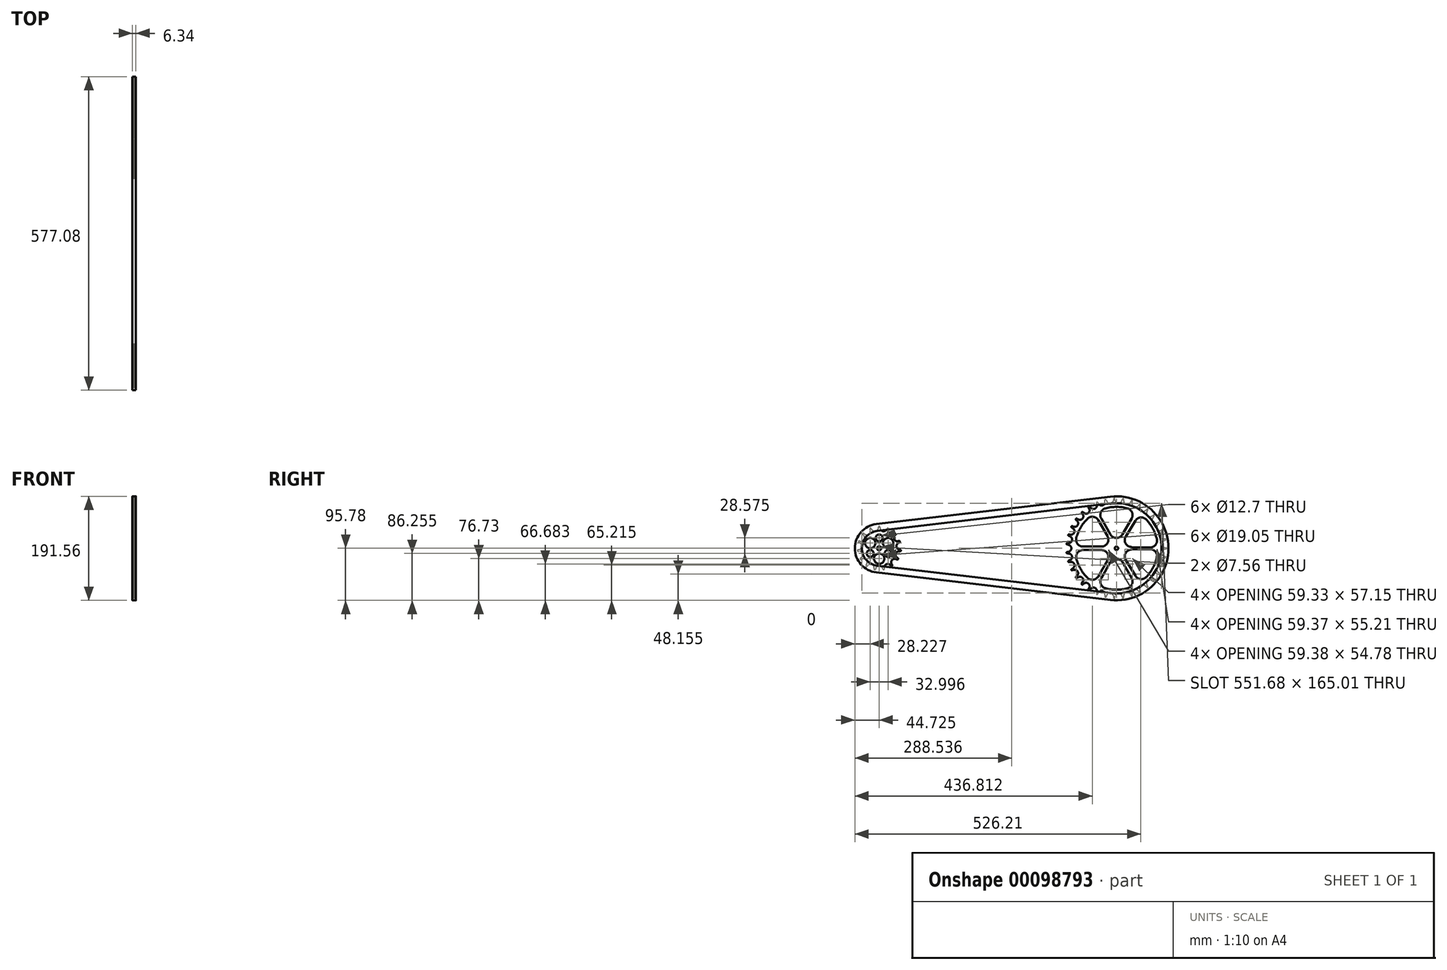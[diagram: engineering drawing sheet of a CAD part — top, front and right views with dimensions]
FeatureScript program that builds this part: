
annotation { "Feature Type Name" : "Feature", "Feature Type Description" : "" }
export const myFeature = defineFeature(function(context is Context, id is Id, definition is map)
    precondition{}
    {
        {
            var Q0;
            Q0=qCreatedBy(makeId("Right.planeOp"),FACE);
            var sketch = newSketch(context, id + "F0", { "sketchPlane" : qUnion([Q0])});
            skPoint(sketch, "E0.0.midPoint", {"position": v(88.9, 0) * mm});
            skArc(sketch, "E1", {"start": v(-53.39, 54.37) * mm, "mid": v(-66, 38.1) * mm, "end": v(-73.78, 19.05) * mm});
            skLineSegment(sketch, "E2", {"start": v(-33.5, 51.66) * mm, "end": v(-16.5, 22.22) * mm});
            skLineSegment(sketch, "E3", {"start": v(-61.48, 3.18) * mm, "end": v(-27.5, 3.18) * mm});
            skArc(sketch, "E4", {"start": v(-27.5, 3.17) * mm, "mid": v(-16.5, 9.52) * mm, "end": v(-16.5, 22.23) * mm});
            skArc(sketch, "E5", {"start": v(-33.5, 51.66) * mm, "mid": v(-42.77, 57.9) * mm, "end": v(-53.39, 54.37) * mm});
            skArc(sketch, "E6", {"start": v(-73.78, 19.05) * mm, "mid": v(-71.52, 8.1) * mm, "end": v(-61.48, 3.17) * mm});
            skArc(sketch, "E7.MirrorCS", {"start": v(-20.4, 73.42) * mm, "mid": v(0, 76.2) * mm, "end": v(20.4, 73.42) * mm});
            skArc(sketch, "E8.MirrorCS", {"start": v(-28, 54.83) * mm, "mid": v(-28.75, 66) * mm, "end": v(-20.4, 73.42) * mm});
            skLineSegment(sketch, "E9.MirrorCS", {"start": v(-28, 54.83) * mm, "end": v(-11, 25.4) * mm});
            skArc(sketch, "E10.MirrorCS", {"start": v(11, 25.4) * mm, "mid": v(0, 19.05) * mm, "end": v(-11, 25.4) * mm});
            skLineSegment(sketch, "E11.MirrorCS", {"start": v(28, 54.83) * mm, "end": v(11, 25.4) * mm});
            skArc(sketch, "E12.MirrorCS", {"start": v(20.4, 73.42) * mm, "mid": v(28.75, 66) * mm, "end": v(28, 54.83) * mm});
            skArc(sketch, "E13.MirrorCS", {"start": v(74.27, 17.03) * mm, "mid": v(67, 36.28) * mm, "end": v(54.85, 52.9) * mm});
            skArc(sketch, "E14.MirrorCS", {"start": v(61.55, 1.5) * mm, "mid": v(71.72, 6.14) * mm, "end": v(74.27, 17.03) * mm});
            skLineSegment(sketch, "E15.MirrorCS", {"start": v(61.55, 1.5) * mm, "end": v(27.57, 2.42) * mm});
            skArc(sketch, "E16.MirrorCS", {"start": v(17.1, 21.77) * mm, "mid": v(16.75, 9.07) * mm, "end": v(27.57, 2.42) * mm});
            skLineSegment(sketch, "E17.MirrorCS", {"start": v(34.9, 50.72) * mm, "end": v(17.1, 21.77) * mm});
            skArc(sketch, "E18.MirrorCS", {"start": v(54.85, 52.9) * mm, "mid": v(44.34, 56.7) * mm, "end": v(34.9, 50.72) * mm});
            skArc(sketch, "E19.MirrorCS", {"start": v(-53.39, -54.37) * mm, "mid": v(-66, -38.1) * mm, "end": v(-73.78, -19.05) * mm});
            skArc(sketch, "E20.MirrorCS", {"start": v(-73.78, -19.05) * mm, "mid": v(-71.52, -8.1) * mm, "end": v(-61.48, -3.17) * mm});
            skLineSegment(sketch, "E21.MirrorCS", {"start": v(-61.48, -3.18) * mm, "end": v(-27.5, -3.18) * mm});
            skArc(sketch, "E22.MirrorCS", {"start": v(-27.5, -3.17) * mm, "mid": v(-16.5, -9.52) * mm, "end": v(-16.5, -22.23) * mm});
            skLineSegment(sketch, "E23.MirrorCS", {"start": v(-33.5, -51.66) * mm, "end": v(-16.5, -22.22) * mm});
            skArc(sketch, "E24.MirrorCS", {"start": v(-33.5, -51.66) * mm, "mid": v(-42.77, -57.9) * mm, "end": v(-53.39, -54.37) * mm});
            skArc(sketch, "E25.MirrorCS", {"start": v(-28, -54.83) * mm, "mid": v(-28.75, -66) * mm, "end": v(-20.4, -73.42) * mm});
            skArc(sketch, "E26.MirrorCS", {"start": v(-20.4, -73.42) * mm, "mid": v(0, -76.2) * mm, "end": v(20.4, -73.42) * mm});
            skArc(sketch, "E27.MirrorCS", {"start": v(20.4, -73.42) * mm, "mid": v(28.75, -66) * mm, "end": v(28, -54.83) * mm});
            skLineSegment(sketch, "E28.MirrorCS", {"start": v(28, -54.83) * mm, "end": v(11, -25.4) * mm});
            skArc(sketch, "E29.MirrorCS", {"start": v(11, -25.4) * mm, "mid": v(0, -19.05) * mm, "end": v(-11, -25.4) * mm});
            skLineSegment(sketch, "E30.MirrorCS", {"start": v(34.9, -50.72) * mm, "end": v(17.1, -21.77) * mm});
            skArc(sketch, "E31.MirrorCS", {"start": v(54.85, -52.9) * mm, "mid": v(44.34, -56.7) * mm, "end": v(34.9, -50.72) * mm});
            skArc(sketch, "E32.MirrorCS", {"start": v(74.27, -17.03) * mm, "mid": v(67, -36.28) * mm, "end": v(54.85, -52.9) * mm});
            skArc(sketch, "E33.MirrorCS", {"start": v(61.55, -1.5) * mm, "mid": v(71.72, -6.14) * mm, "end": v(74.27, -17.03) * mm});
            skLineSegment(sketch, "E34.MirrorCS", {"start": v(61.55, -1.5) * mm, "end": v(27.57, -2.42) * mm});
            skArc(sketch, "E35.MirrorCS", {"start": v(17.1, -21.77) * mm, "mid": v(16.75, -9.07) * mm, "end": v(27.57, -2.42) * mm});
            skLineSegment(sketch, "E36.MirrorCS", {"start": v(-28, -54.83) * mm, "end": v(-11, -25.4) * mm});
            skArc(sketch, "E37", {"start": v(-62.06, 66.67) * mm, "mid": v(-63.62, 66.56) * mm, "end": v(-63.79, 65.01) * mm});
            skArc(sketch, "E38.trimOffspring", {"start": v(-70.02, 53.03) * mm, "mid": v(-62.46, 54.56) * mm, "end": v(-61.95, 62.26) * mm});
            skArc(sketch, "E39.MirrorCS", {"start": v(-74.4, 52.54) * mm, "mid": v(-74.5, 54.1) * mm, "end": v(-72.99, 54.48) * mm});
            skPoint(sketch, "E40.orphan", {"position": v(-81.26, 58.5) * mm});
            skArc(sketch, "E41.MirrorCS", {"start": v(-36.12, 80.06) * mm, "mid": v(-39.3, 73.03) * mm, "end": v(-46.92, 74.26) * mm});
            skArc(sketch, "E42.MirrorCS", {"start": v(-51.18, 75.34) * mm, "mid": v(-50.74, 76.83) * mm, "end": v(-49.19, 76.65) * mm});
            skArc(sketch, "E43", {"start": v(-59.4, 64.7) * mm, "mid": v(-51.8, 64.95) * mm, "end": v(-49.87, 72.3) * mm});
            skArc(sketch, "E44.MirrorCS", {"start": v(-34.67, 84.22) * mm, "mid": v(-36.16, 84.68) * mm, "end": v(-36.87, 83.28) * mm});
            skPoint(sketch, "E45.orphan", {"position": v(-38.96, 92.24) * mm});
            skArc(sketch, "E46.MirrorCS", {"start": v(-21.28, 85.22) * mm, "mid": v(-25.66, 79) * mm, "end": v(-32.86, 81.46) * mm});
            skArc(sketch, "E47.MirrorCS", {"start": v(-21.44, 88.52) * mm, "mid": v(-20.5, 89.76) * mm, "end": v(-19.1, 89.05) * mm});
            skArc(sketch, "E48.MirrorCS", {"start": v(-5.68, 87.65) * mm, "mid": v(-11.12, 82.18) * mm, "end": v(-17.83, 86) * mm});
            skArc(sketch, "E49.MirrorCS", {"start": v(-2.86, 91.03) * mm, "mid": v(-4.1, 91.98) * mm, "end": v(-5.25, 90.93) * mm});
            skArc(sketch, "E50.MirrorCS", {"start": v(-84.2, 25.04) * mm, "mid": v(-77.65, 29.13) * mm, "end": v(-79.88, 36.52) * mm});
            skArc(sketch, "E51.MirrorCS", {"start": v(-72.1, 50.17) * mm, "mid": v(-71.31, 42.6) * mm, "end": v(-78.35, 39.7) * mm});
            skArc(sketch, "E52.MirrorCS", {"start": v(-81.53, 40.6) * mm, "mid": v(-82.95, 39.96) * mm, "end": v(-82.57, 38.45) * mm});
            skArc(sketch, "E53.MirrorCS", {"start": v(-88.12, 23.04) * mm, "mid": v(-88.77, 24.46) * mm, "end": v(-87.48, 25.35) * mm});
            skArc(sketch, "E54.MirrorCS", {"start": v(-87.3, 9.64) * mm, "mid": v(-81.74, 14.82) * mm, "end": v(-85.13, 21.63) * mm});
            skArc(sketch, "E55.MirrorCS", {"start": v(-90.6, 9.36) * mm, "mid": v(-91.7, 8.26) * mm, "end": v(-90.81, 6.98) * mm});
            skArc(sketch, "E56.MirrorCS", {"start": v(-87.62, -6.15) * mm, "mid": v(-82.93, -0.02) * mm, "end": v(-87.62, 6.11) * mm});
            skArc(sketch, "E57.MirrorCS", {"start": v(-90.6, -9.4) * mm, "mid": v(-91.7, -8.3) * mm, "end": v(-90.8, -7) * mm});
            skArc(sketch, "E58.MirrorCS", {"start": v(-87.31, -9.62) * mm, "mid": v(-81.75, -14.8) * mm, "end": v(-85.15, -21.6) * mm});
            skArc(sketch, "E59.MirrorCS", {"start": v(-88.14, -23.02) * mm, "mid": v(-88.8, -24.44) * mm, "end": v(-87.5, -25.33) * mm});
            skArc(sketch, "E60.MirrorCS", {"start": v(-84.22, -25.02) * mm, "mid": v(-77.68, -29.12) * mm, "end": v(-79.92, -36.5) * mm});
            skArc(sketch, "E61.MirrorCS", {"start": v(-81.57, -40.59) * mm, "mid": v(-83, -39.94) * mm, "end": v(-82.6, -38.43) * mm});
            skArc(sketch, "E62.MirrorCS", {"start": v(-72.1, -50.18) * mm, "mid": v(-71.32, -42.61) * mm, "end": v(-78.36, -39.72) * mm});
            skArc(sketch, "E63.MirrorCS", {"start": v(-74.42, -52.5) * mm, "mid": v(-74.53, -54.06) * mm, "end": v(-73.02, -54.44) * mm});
            skArc(sketch, "E64.MirrorCS", {"start": v(-70.05, -53) * mm, "mid": v(-62.48, -54.53) * mm, "end": v(-61.99, -62.23) * mm});
            skArc(sketch, "E65.MirrorCS", {"start": v(-62.1, -66.63) * mm, "mid": v(-63.65, -66.53) * mm, "end": v(-63.82, -64.98) * mm});
            skArc(sketch, "E66.MirrorCS", {"start": v(-59.43, -64.68) * mm, "mid": v(-51.83, -64.92) * mm, "end": v(-49.91, -72.28) * mm});
            skArc(sketch, "E67.MirrorCS", {"start": v(-51.23, -75.3) * mm, "mid": v(-50.78, -76.8) * mm, "end": v(-49.23, -76.63) * mm});
            skArc(sketch, "E68.MirrorCS", {"start": v(-46.96, -74.23) * mm, "mid": v(-39.34, -73) * mm, "end": v(-36.16, -80.04) * mm});
            skArc(sketch, "E69.MirrorCS", {"start": v(-21.28, -85.22) * mm, "mid": v(-25.67, -79) * mm, "end": v(-32.87, -81.45) * mm});
            skArc(sketch, "E70.MirrorCS", {"start": v(-34.67, -84.22) * mm, "mid": v(-36.17, -84.67) * mm, "end": v(-36.87, -83.28) * mm});
            skArc(sketch, "E71.MirrorCS", {"start": v(-21.45, -88.52) * mm, "mid": v(-20.5, -89.76) * mm, "end": v(-19.11, -89.05) * mm});
            skArc(sketch, "E72.MirrorCS", {"start": v(-5.68, -87.65) * mm, "mid": v(-11.13, -82.18) * mm, "end": v(-17.83, -86) * mm});
            skArc(sketch, "E73.MirrorCS", {"start": v(-2.86, -91.03) * mm, "mid": v(-4.1, -91.98) * mm, "end": v(-5.25, -90.93) * mm});
            skArc(sketch, "E74.MirrorCS", {"start": v(-2.2, -87.82) * mm, "mid": v(3.69, -83) * mm, "end": v(9.97, -87.28) * mm});
            skArc(sketch, "E75.MirrorCS", {"start": v(11.02, -90.44) * mm, "mid": v(12.34, -91.28) * mm, "end": v(13.4, -90.12) * mm});
            skArc(sketch, "E76.MirrorCS", {"start": v(13.48, -86.8) * mm, "mid": v(18.41, -80.86) * mm, "end": v(25.43, -84.07) * mm});
            skArc(sketch, "E77.MirrorCS", {"start": v(29.26, -86.25) * mm, "mid": v(28.43, -87.58) * mm, "end": v(26.98, -86.99) * mm});
            skArc(sketch, "E78.MirrorCS", {"start": v(28.8, -82.98) * mm, "mid": v(32.61, -76.4) * mm, "end": v(40, -78.2) * mm});
            skArc(sketch, "E79.MirrorCS", {"start": v(42.05, -80.8) * mm, "mid": v(43.58, -81.1) * mm, "end": v(44.16, -79.66) * mm});
            skArc(sketch, "E80.MirrorCS", {"start": v(53.4, -69.74) * mm, "mid": v(45.7, -69.2) * mm, "end": v(43.16, -76.5) * mm});
            skArc(sketch, "E81.MirrorCS", {"start": v(57.74, -70.44) * mm, "mid": v(57.43, -71.97) * mm, "end": v(55.87, -71.93) * mm});
            skArc(sketch, "E82.MirrorCS", {"start": v(64.96, -59.12) * mm, "mid": v(57.41, -60.03) * mm, "end": v(56.16, -67.54) * mm});
            skArc(sketch, "E83.MirrorCS", {"start": v(67.8, -60.82) * mm, "mid": v(69.34, -60.58) * mm, "end": v(69.37, -59.02) * mm});
            skArc(sketch, "E84.MirrorCS", {"start": v(74.5, -46.53) * mm, "mid": v(67.1, -48.73) * mm, "end": v(67.3, -56.45) * mm});
            skArc(sketch, "E85.MirrorCS", {"start": v(-2.14, 87.8) * mm, "mid": v(3.74, 82.99) * mm, "end": v(10.03, 87.26) * mm});
            skArc(sketch, "E86.MirrorCS", {"start": v(11.03, 90.4) * mm, "mid": v(12.35, 91.24) * mm, "end": v(13.4, 90.09) * mm});
            skArc(sketch, "E87.MirrorCS", {"start": v(13.54, 86.79) * mm, "mid": v(18.47, 80.85) * mm, "end": v(25.49, 84.06) * mm});
            skArc(sketch, "E88.MirrorCS", {"start": v(29.32, 86.23) * mm, "mid": v(28.49, 87.56) * mm, "end": v(27.04, 86.97) * mm});
            skArc(sketch, "E89.MirrorCS", {"start": v(40.06, 78.17) * mm, "mid": v(32.67, 76.38) * mm, "end": v(28.86, 82.96) * mm});
            skArc(sketch, "E90.MirrorCS", {"start": v(42.1, 80.76) * mm, "mid": v(43.63, 81.08) * mm, "end": v(44.21, 79.63) * mm});
            skArc(sketch, "E91.MirrorCS", {"start": v(53.4, 69.74) * mm, "mid": v(45.7, 69.2) * mm, "end": v(43.17, 76.5) * mm});
            skArc(sketch, "E92.MirrorCS", {"start": v(56.17, 67.53) * mm, "mid": v(57.42, 60.03) * mm, "end": v(64.97, 59.1) * mm});
            skArc(sketch, "E93.MirrorCS", {"start": v(57.75, 70.43) * mm, "mid": v(57.44, 71.96) * mm, "end": v(55.88, 71.92) * mm});
            skArc(sketch, "E94.MirrorCS", {"start": v(67.8, 60.81) * mm, "mid": v(69.34, 60.57) * mm, "end": v(69.38, 59.01) * mm});
            skArc(sketch, "E95.MirrorCS", {"start": v(74.5, 46.52) * mm, "mid": v(67.1, 48.72) * mm, "end": v(67.3, 56.44) * mm});
            skArc(sketch, "E96.MirrorCS", {"start": v(78.82, 45.64) * mm, "mid": v(79.07, 47.18) * mm, "end": v(77.6, 47.7) * mm});
            skArc(sketch, "E97.MirrorCS", {"start": v(81.6, 32.5) * mm, "mid": v(74.86, 36.02) * mm, "end": v(76.32, 43.48) * mm});
            skArc(sketch, "E98.MirrorCS", {"start": v(84.85, 33.1) * mm, "mid": v(86.2, 32.34) * mm, "end": v(85.69, 30.87) * mm});
            skArc(sketch, "E99.MirrorCS", {"start": v(82.84, 29.19) * mm, "mid": v(79.95, 22.03) * mm, "end": v(86.1, 17.37) * mm});
            skArc(sketch, "E100.MirrorCS", {"start": v(89.83, 15.03) * mm, "mid": v(90.6, 16.38) * mm, "end": v(89.4, 17.38) * mm});
            skArc(sketch, "E101.MirrorCS", {"start": v(86.73, 13.88) * mm, "mid": v(82.74, 7.41) * mm, "end": v(87.82, 1.75) * mm});
            skArc(sketch, "E102.MirrorCS", {"start": v(91.07, 1.18) * mm, "mid": v(92.07, -0.02) * mm, "end": v(91.07, -1.22) * mm});
            skArc(sketch, "E103.MirrorCS", {"start": v(86.71, -14) * mm, "mid": v(82.6, -7.47) * mm, "end": v(87.82, -1.8) * mm});
            skArc(sketch, "E104.MirrorCS", {"start": v(89.38, -17.5) * mm, "mid": v(90.58, -16.5) * mm, "end": v(89.81, -15.15) * mm});
            skArc(sketch, "E105.MirrorCS", {"start": v(86.08, -17.48) * mm, "mid": v(80.07, -22.14) * mm, "end": v(82.83, -29.22) * mm});
            skArc(sketch, "E106.MirrorCS", {"start": v(85.67, -30.9) * mm, "mid": v(86.2, -32.38) * mm, "end": v(84.83, -33.15) * mm});
            skArc(sketch, "E107.MirrorCS", {"start": v(81.59, -32.54) * mm, "mid": v(74.7, -36.02) * mm, "end": v(76.26, -43.58) * mm});
            skArc(sketch, "E108.MirrorCS", {"start": v(77.53, -47.8) * mm, "mid": v(79, -47.29) * mm, "end": v(78.76, -45.74) * mm});
            skLineSegment(sketch, "E109", {"start": v(-88.14, -23.02) * mm, "end": v(-85.15, -21.6) * mm});
            skLineSegment(sketch, "E110", {"start": v(-87.5, -25.33) * mm, "end": v(-84.22, -25.02) * mm});
            skLineSegment(sketch, "E111", {"start": v(-82.6, -38.43) * mm, "end": v(-79.92, -36.5) * mm});
            skLineSegment(sketch, "E112", {"start": v(-81.57, -40.59) * mm, "end": v(-78.36, -39.72) * mm});
            skLineSegment(sketch, "E113", {"start": v(-74.42, -52.5) * mm, "end": v(-72.1, -50.18) * mm});
            skLineSegment(sketch, "E114", {"start": v(-73.02, -54.44) * mm, "end": v(-70.05, -53) * mm});
            skLineSegment(sketch, "E115", {"start": v(-63.82, -64.98) * mm, "end": v(-61.99, -62.23) * mm});
            skLineSegment(sketch, "E116", {"start": v(-62.1, -66.63) * mm, "end": v(-59.43, -64.68) * mm});
            skLineSegment(sketch, "E117", {"start": v(-51.23, -75.3) * mm, "end": v(-49.91, -72.28) * mm});
            skLineSegment(sketch, "E118", {"start": v(-49.23, -76.63) * mm, "end": v(-46.96, -74.23) * mm});
            skLineSegment(sketch, "E119", {"start": v(-36.16, -80.04) * mm, "end": v(-36.87, -83.28) * mm});
            skLineSegment(sketch, "E120", {"start": v(-34.67, -84.22) * mm, "end": v(-32.87, -81.45) * mm});
            skLineSegment(sketch, "E121", {"start": v(-21.28, -85.22) * mm, "end": v(-21.45, -88.52) * mm});
            skLineSegment(sketch, "E122", {"start": v(-19.11, -89.05) * mm, "end": v(-17.83, -86) * mm});
            skLineSegment(sketch, "E123", {"start": v(-5.68, -87.65) * mm, "end": v(-5.25, -90.93) * mm});
            skLineSegment(sketch, "E124", {"start": v(-2.86, -91.03) * mm, "end": v(-2.2, -87.82) * mm});
            skLineSegment(sketch, "E125", {"start": v(9.97, -87.28) * mm, "end": v(11.02, -90.44) * mm});
            skLineSegment(sketch, "E126", {"start": v(13.4, -90.12) * mm, "end": v(13.48, -86.8) * mm});
            skLineSegment(sketch, "E127", {"start": v(25.43, -84.07) * mm, "end": v(26.98, -86.99) * mm});
            skLineSegment(sketch, "E128", {"start": v(29.26, -86.25) * mm, "end": v(28.8, -82.98) * mm});
            skLineSegment(sketch, "E129", {"start": v(40, -78.2) * mm, "end": v(42.05, -80.8) * mm});
            skLineSegment(sketch, "E130", {"start": v(44.16, -79.66) * mm, "end": v(43.16, -76.5) * mm});
            skLineSegment(sketch, "E131", {"start": v(53.4, -69.74) * mm, "end": v(55.87, -71.93) * mm});
            skLineSegment(sketch, "E132", {"start": v(57.74, -70.44) * mm, "end": v(56.16, -67.54) * mm});
            skLineSegment(sketch, "E133", {"start": v(64.96, -59.12) * mm, "end": v(67.8, -60.82) * mm});
            skLineSegment(sketch, "E134", {"start": v(69.37, -59.02) * mm, "end": v(67.3, -56.45) * mm});
            skLineSegment(sketch, "E135", {"start": v(74.5, -46.53) * mm, "end": v(77.53, -47.8) * mm});
            skLineSegment(sketch, "E136", {"start": v(76.26, -43.58) * mm, "end": v(78.76, -45.74) * mm});
            skLineSegment(sketch, "E137", {"start": v(81.59, -32.54) * mm, "end": v(84.83, -33.15) * mm});
            skLineSegment(sketch, "E138", {"start": v(82.83, -29.22) * mm, "end": v(85.67, -30.9) * mm});
            skLineSegment(sketch, "E139", {"start": v(86.08, -17.48) * mm, "end": v(89.38, -17.5) * mm});
            skLineSegment(sketch, "E140", {"start": v(86.71, -14) * mm, "end": v(89.81, -15.15) * mm});
            skLineSegment(sketch, "E141", {"start": v(87.82, -1.8) * mm, "end": v(91.07, -1.22) * mm});
            skLineSegment(sketch, "E142", {"start": v(87.82, 1.75) * mm, "end": v(91.07, 1.18) * mm});
            skLineSegment(sketch, "E143", {"start": v(86.73, 13.88) * mm, "end": v(89.83, 15.03) * mm});
            skLineSegment(sketch, "E144", {"start": v(86.1, 17.37) * mm, "end": v(89.4, 17.38) * mm});
            skLineSegment(sketch, "E145", {"start": v(82.84, 29.19) * mm, "end": v(85.69, 30.87) * mm});
            skLineSegment(sketch, "E146", {"start": v(81.6, 32.5) * mm, "end": v(84.85, 33.1) * mm});
            skLineSegment(sketch, "E147", {"start": v(76.32, 43.48) * mm, "end": v(78.82, 45.64) * mm});
            skLineSegment(sketch, "E148", {"start": v(74.5, 46.52) * mm, "end": v(77.6, 47.7) * mm});
            skLineSegment(sketch, "E149", {"start": v(67.3, 56.44) * mm, "end": v(69.38, 59.01) * mm});
            skLineSegment(sketch, "E150", {"start": v(64.97, 59.1) * mm, "end": v(67.8, 60.81) * mm});
            skLineSegment(sketch, "E151", {"start": v(56.17, 67.53) * mm, "end": v(57.75, 70.43) * mm});
            skLineSegment(sketch, "E152", {"start": v(55.88, 71.92) * mm, "end": v(53.4, 69.74) * mm});
            skLineSegment(sketch, "E153", {"start": v(43.17, 76.5) * mm, "end": v(44.21, 79.63) * mm});
            skLineSegment(sketch, "E154", {"start": v(42.1, 80.76) * mm, "end": v(40.06, 78.17) * mm});
            skLineSegment(sketch, "E155", {"start": v(28.86, 82.96) * mm, "end": v(29.32, 86.23) * mm});
            skLineSegment(sketch, "E156", {"start": v(27.04, 86.97) * mm, "end": v(25.49, 84.06) * mm});
            skLineSegment(sketch, "E157", {"start": v(13.54, 86.79) * mm, "end": v(13.4, 90.09) * mm});
            skLineSegment(sketch, "E158", {"start": v(10.03, 87.26) * mm, "end": v(11.03, 90.4) * mm});
            skLineSegment(sketch, "E159", {"start": v(-2.14, 87.8) * mm, "end": v(-2.86, 91.03) * mm});
            skLineSegment(sketch, "E160", {"start": v(-5.25, 90.93) * mm, "end": v(-5.68, 87.65) * mm});
            skLineSegment(sketch, "E161", {"start": v(-19.1, 89.05) * mm, "end": v(-17.83, 86) * mm});
            skLineSegment(sketch, "E162", {"start": v(-21.28, 85.22) * mm, "end": v(-21.44, 88.52) * mm});
            skLineSegment(sketch, "E163", {"start": v(-34.67, 84.22) * mm, "end": v(-32.86, 81.46) * mm});
            skLineSegment(sketch, "E164", {"start": v(-36.12, 80.06) * mm, "end": v(-36.87, 83.28) * mm});
            skLineSegment(sketch, "E165", {"start": v(-46.92, 74.26) * mm, "end": v(-49.19, 76.65) * mm});
            skLineSegment(sketch, "E166", {"start": v(-51.18, 75.34) * mm, "end": v(-49.87, 72.3) * mm});
            skLineSegment(sketch, "E167", {"start": v(-59.4, 64.7) * mm, "end": v(-62.06, 66.67) * mm});
            skLineSegment(sketch, "E168", {"start": v(-61.95, 62.26) * mm, "end": v(-63.79, 65.01) * mm});
            skLineSegment(sketch, "E169", {"start": v(-70.02, 53.03) * mm, "end": v(-72.99, 54.48) * mm});
            skLineSegment(sketch, "E170", {"start": v(-74.4, 52.54) * mm, "end": v(-72.1, 50.17) * mm});
            skLineSegment(sketch, "E171", {"start": v(-78.35, 39.7) * mm, "end": v(-81.53, 40.6) * mm});
            skLineSegment(sketch, "E172", {"start": v(-82.57, 38.45) * mm, "end": v(-79.88, 36.52) * mm});
            skLineSegment(sketch, "E173", {"start": v(-84.2, 25.04) * mm, "end": v(-87.48, 25.35) * mm});
            skLineSegment(sketch, "E174", {"start": v(-88.12, 23.04) * mm, "end": v(-85.13, 21.63) * mm});
            skLineSegment(sketch, "E175", {"start": v(-87.3, 9.64) * mm, "end": v(-90.6, 9.36) * mm});
            skLineSegment(sketch, "E176", {"start": v(-90.81, 6.98) * mm, "end": v(-87.62, 6.11) * mm});
            skLineSegment(sketch, "E177", {"start": v(-90.8, -7) * mm, "end": v(-87.62, -6.15) * mm});
            skLineSegment(sketch, "E178", {"start": v(-90.6, -9.4) * mm, "end": v(-87.31, -9.62) * mm});
            skCircle(sketch, "E179", {"center": v(0, 0) * mm, "radius": 3.17 * mm});
            skPoint(sketch, "E180.0.midPoint", {"position": v(-436.58, 37.7) * mm});
            skArc(sketch, "E181", {"start": v(-430.2, -37.19) * mm, "mid": v(-436.58, -32.02) * mm, "end": v(-442.95, -37.19) * mm});
            skArc(sketch, "E182", {"start": v(-415.76, -31.48) * mm, "mid": v(-423.35, -29.35) * mm, "end": v(-427.16, -36.25) * mm});
            skLineSegment(sketch, "E183", {"start": v(-427.16, -36.25) * mm, "end": v(-426.94, -37.59) * mm});
            skPoint(sketch, "E184", {"position": v(-429.91, -38.22) * mm});
            skPoint(sketch, "E185", {"position": v(-428.43, -37.9) * mm});
            skLineSegment(sketch, "E186", {"start": v(-428.43, -37.9) * mm, "end": v(-427.72, -40.52) * mm});
            skArc(sketch, "E187", {"start": v(-429.91, -38.22) * mm, "mid": v(-428.13, -39.32) * mm, "end": v(-426.94, -37.59) * mm});
            skArc(sketch, "E188.MirrorCS", {"start": v(-412.63, -30.52) * mm, "mid": v(-413, -32.6) * mm, "end": v(-415.09, -32.3) * mm});
            skLineSegment(sketch, "E189", {"start": v(-430.2, -37.19) * mm, "end": v(-429.91, -38.22) * mm});
            skLineSegment(sketch, "E190.MirrorCS", {"start": v(-413.2, -29.62) * mm, "end": v(-412.63, -30.52) * mm});
            skArc(sketch, "E191.MirrorCS", {"start": v(-413.2, -29.62) * mm, "mid": v(-412.78, -21.43) * mm, "end": v(-404.67, -20.15) * mm});
            skArc(sketch, "E192.MirrorCS", {"start": v(-443.24, -38.22) * mm, "mid": v(-445.02, -39.32) * mm, "end": v(-446.2, -37.59) * mm});
            skLineSegment(sketch, "E193.MirrorCS", {"start": v(-442.95, -37.19) * mm, "end": v(-443.24, -38.22) * mm});
            skLineSegment(sketch, "E194.MirrorCS", {"start": v(-445.99, -36.25) * mm, "end": v(-446.2, -37.59) * mm});
            skArc(sketch, "E195.MirrorCS", {"start": v(-457.39, -31.48) * mm, "mid": v(-449.8, -29.35) * mm, "end": v(-445.99, -36.25) * mm});
            skArc(sketch, "E196.MirrorCS", {"start": v(-460.52, -30.52) * mm, "mid": v(-460.14, -32.6) * mm, "end": v(-458.06, -32.3) * mm});
            skLineSegment(sketch, "E197.MirrorCS", {"start": v(-457.21, -31.25) * mm, "end": v(-458.06, -32.3) * mm});
            skLineSegment(sketch, "E198.MirrorCS", {"start": v(-459.94, -29.62) * mm, "end": v(-460.52, -30.52) * mm});
            skArc(sketch, "E199.MirrorCS", {"start": v(-459.94, -29.62) * mm, "mid": v(-460.37, -21.43) * mm, "end": v(-468.48, -20.15) * mm});
            skLineSegment(sketch, "E200", {"start": v(-415.09, -32.3) * mm, "end": v(-415.76, -31.48) * mm});
            skLineSegment(sketch, "E201.MirrorCS", {"start": v(-404.67, -20.15) * mm, "end": v(-403.72, -20.62) * mm});
            skArc(sketch, "E202.MirrorCS", {"start": v(-403.72, -20.62) * mm, "mid": v(-401.7, -20.03) * mm, "end": v(-402.2, -18) * mm});
            skLineSegment(sketch, "E203.MirrorCS", {"start": v(-402.2, -18) * mm, "end": v(-403.1, -17.4) * mm});
            skArc(sketch, "E204.MirrorCS", {"start": v(-403.1, -17.4) * mm, "mid": v(-406, -10.09) * mm, "end": v(-399.54, -5.57) * mm});
            skArc(sketch, "E205.MirrorCS", {"start": v(-398.92, -2.45) * mm, "mid": v(-404.73, 3.35) * mm, "end": v(-400.26, 10.23) * mm});
            skLineSegment(sketch, "E206.MirrorCS", {"start": v(-399.54, -5.57) * mm, "end": v(-398.19, -5.65) * mm});
            skLineSegment(sketch, "E207.MirrorCS", {"start": v(-398.92, -2.45) * mm, "end": v(-397.87, -2.63) * mm});
            skArc(sketch, "E208.MirrorCS", {"start": v(-399.26, 10.62) * mm, "mid": v(-398.35, 12.51) * mm, "end": v(-400.2, 13.5) * mm});
            skArc(sketch, "E209.MirrorCS", {"start": v(-397.87, -2.63) * mm, "mid": v(-396.58, -4.3) * mm, "end": v(-398.19, -5.65) * mm});
            skLineSegment(sketch, "E210", {"start": v(-399.26, 10.62) * mm, "end": v(-400.26, 10.23) * mm});
            skArc(sketch, "E211.MirrorCS", {"start": v(-407.44, 24) * mm, "mid": v(-408.77, 16.22) * mm, "end": v(-401.5, 13.15) * mm});
            skLineSegment(sketch, "E212.MirrorCS", {"start": v(-401.5, 13.15) * mm, "end": v(-400.2, 13.5) * mm});
            skArc(sketch, "E213.MirrorCS", {"start": v(-419.88, 33.83) * mm, "mid": v(-417.75, 25.9) * mm, "end": v(-409.56, 26.34) * mm});
            skArc(sketch, "E214.MirrorCS", {"start": v(-438.07, 37.7) * mm, "mid": v(-443.23, 31.33) * mm, "end": v(-450.54, 35.05) * mm});
            skArc(sketch, "E215.MirrorCS", {"start": v(-419.5, 34.84) * mm, "mid": v(-420.3, 36.78) * mm, "end": v(-422.28, 36.07) * mm});
            skArc(sketch, "E216.MirrorCS", {"start": v(-408.72, 27) * mm, "mid": v(-406.63, 26.85) * mm, "end": v(-406.69, 24.75) * mm});
            skArc(sketch, "E217.MirrorCS", {"start": v(-451.04, 36) * mm, "mid": v(-453.02, 36.7) * mm, "end": v(-453.81, 34.76) * mm});
            skArc(sketch, "E218.MirrorCS", {"start": v(-466.34, 24.88) * mm, "mid": v(-466.4, 26.98) * mm, "end": v(-464.3, 27.14) * mm});
            skArc(sketch, "E219.MirrorCS", {"start": v(-438, 38.77) * mm, "mid": v(-436.49, 40.22) * mm, "end": v(-434.97, 38.77) * mm});
            skArc(sketch, "E220.MirrorCS", {"start": v(-463.48, 26.46) * mm, "mid": v(-455.62, 25.96) * mm, "end": v(-453.32, 33.5) * mm});
            skArc(sketch, "E221.MirrorCS", {"start": v(-465.6, 24.12) * mm, "mid": v(-464.3, 16.01) * mm, "end": v(-471.97, 13.07) * mm});
            skArc(sketch, "E222.MirrorCS", {"start": v(-422.76, 35.12) * mm, "mid": v(-429.74, 31.46) * mm, "end": v(-434.9, 37.41) * mm});
            skLineSegment(sketch, "E223", {"start": v(-407.44, 24) * mm, "end": v(-406.69, 24.75) * mm});
            skLineSegment(sketch, "E224", {"start": v(-419.88, 33.83) * mm, "end": v(-419.5, 34.84) * mm});
            skLineSegment(sketch, "E225", {"start": v(-409.56, 26.34) * mm, "end": v(-408.72, 27) * mm});
            skLineSegment(sketch, "E226", {"start": v(-422.76, 35.12) * mm, "end": v(-422.28, 36.07) * mm});
            skLineSegment(sketch, "E227", {"start": v(-434.9, 37.41) * mm, "end": v(-434.97, 38.77) * mm});
            skLineSegment(sketch, "E228", {"start": v(-451.04, 36) * mm, "end": v(-450.54, 35.05) * mm});
            skLineSegment(sketch, "E229", {"start": v(-438.07, 37.7) * mm, "end": v(-438, 38.77) * mm});
            skLineSegment(sketch, "E230", {"start": v(-453.81, 34.76) * mm, "end": v(-453.32, 33.5) * mm});
            skLineSegment(sketch, "E231", {"start": v(-464.3, 27.14) * mm, "end": v(-463.48, 26.46) * mm});
            skLineSegment(sketch, "E232", {"start": v(-466.34, 24.88) * mm, "end": v(-465.6, 24.12) * mm});
            skArc(sketch, "E233.MirrorCS", {"start": v(-469.43, -20.62) * mm, "mid": v(-471.45, -20.03) * mm, "end": v(-470.95, -18) * mm});
            skArc(sketch, "E234.MirrorCS", {"start": v(-475.28, -2.63) * mm, "mid": v(-476.57, -4.3) * mm, "end": v(-474.96, -5.65) * mm});
            skArc(sketch, "E235.MirrorCS", {"start": v(-473.9, -5.6) * mm, "mid": v(-467.24, -9.81) * mm, "end": v(-469.81, -17.26) * mm});
            skArc(sketch, "E236.MirrorCS", {"start": v(-474.23, -2.45) * mm, "mid": v(-468.42, 3.35) * mm, "end": v(-472.9, 10.23) * mm});
            skArc(sketch, "E237.MirrorCS", {"start": v(-473.89, 10.62) * mm, "mid": v(-474.8, 12.51) * mm, "end": v(-472.95, 13.5) * mm});
            skLineSegment(sketch, "E238", {"start": v(-472.95, 13.5) * mm, "end": v(-471.97, 13.07) * mm});
            skLineSegment(sketch, "E239", {"start": v(-473.89, 10.62) * mm, "end": v(-472.9, 10.23) * mm});
            skLineSegment(sketch, "E240", {"start": v(-475.28, -2.63) * mm, "end": v(-474.23, -2.45) * mm});
            skLineSegment(sketch, "E241", {"start": v(-474.96, -5.65) * mm, "end": v(-473.9, -5.6) * mm});
            skLineSegment(sketch, "E242", {"start": v(-470.95, -18) * mm, "end": v(-469.81, -17.26) * mm});
            skLineSegment(sketch, "E243", {"start": v(-469.43, -20.62) * mm, "end": v(-468.48, -20.15) * mm});
            skCircle(sketch, "E244", {"center": v(-436.58, 0) * mm, "radius": 3.78 * mm});
            skCircle(sketch, "E245", {"center": v(-453.07, 9.53) * mm, "radius": 9.53 * mm});
            skCircle(sketch, "E246", {"center": v(-420.08, 9.52) * mm, "radius": 9.53 * mm});
            skCircle(sketch, "E247", {"center": v(-436.58, -19.05) * mm, "radius": 9.53 * mm});
            skCircle(sketch, "E248", {"center": v(-436.58, 19.05) * mm, "radius": 6.35 * mm});
            skCircle(sketch, "E249", {"center": v(-453.07, -9.53) * mm, "radius": 6.35 * mm});
            skCircle(sketch, "E250", {"center": v(-420.08, -9.53) * mm, "radius": 6.35 * mm});
            skLineSegment(sketch, "E251", {"start": v(-436.58, 0) * mm, "end": v(0, 0) * mm});
            skSolve(sketch);
        }
        {
            var Q0;
            Q0 = qSketchRegion(id + "F0", true);
            extrude(context, id + "F1", {"entities" : qUnion([Q0]), "depth" : 3.17 * mm, "symmetric" : true});
        }
        {
            var Q0;
            Q0 = qSketchRegion(id + "F0", true);
            extrude(context, id + "F2", {"entities" : qUnion([Q0]), "depth" : 3.17 * mm, "symmetric" : true});
        }
        {
            var Q0;
            Q0=qCreatedBy(makeId("Right.planeOp"),FACE);
            var sketch = newSketch(context, id + "F3", { "sketchPlane" : qUnion([Q0])});
            skArc(sketch, "E252", {"start": v(-9.71, -82.5) * mm, "mid": v(83.08, 0) * mm, "end": v(-9.71, 82.5) * mm});
            skArc(sketch, "E253", {"start": v(-11.2, -95.12) * mm, "mid": v(95.78, 0) * mm, "end": v(-11.2, 95.12) * mm});
            skArc(sketch, "E254", {"start": v(-440.32, 31.8) * mm, "mid": v(-468.6, -0.12) * mm, "end": v(-440.08, -31.84) * mm});
            skArc(sketch, "E255", {"start": v(-441.8, 44.42) * mm, "mid": v(-481.3, 0) * mm, "end": v(-441.8, -44.42) * mm});
            skLineSegment(sketch, "E256", {"start": v(-441.8, 44.42) * mm, "end": v(-11.2, 95.12) * mm});
            skLineSegment(sketch, "E257", {"start": v(-441.8, -44.42) * mm, "end": v(-11.2, -95.12) * mm});
            skLineSegment(sketch, "E258", {"start": v(-440.32, 31.8) * mm, "end": v(-9.71, 82.5) * mm});
            skLineSegment(sketch, "E259", {"start": v(-440.56, -31.78) * mm, "end": v(0, -83.65) * mm});
            skSolve(sketch);
        }
        {
            var Q0;
            Q0 = qSketchRegion(id + "F3", true);
            extrude(context, id + "F4", {"entities" : qUnion([Q0]), "depth" : 6.35 * mm, "symmetric" : true});
        }
    });
